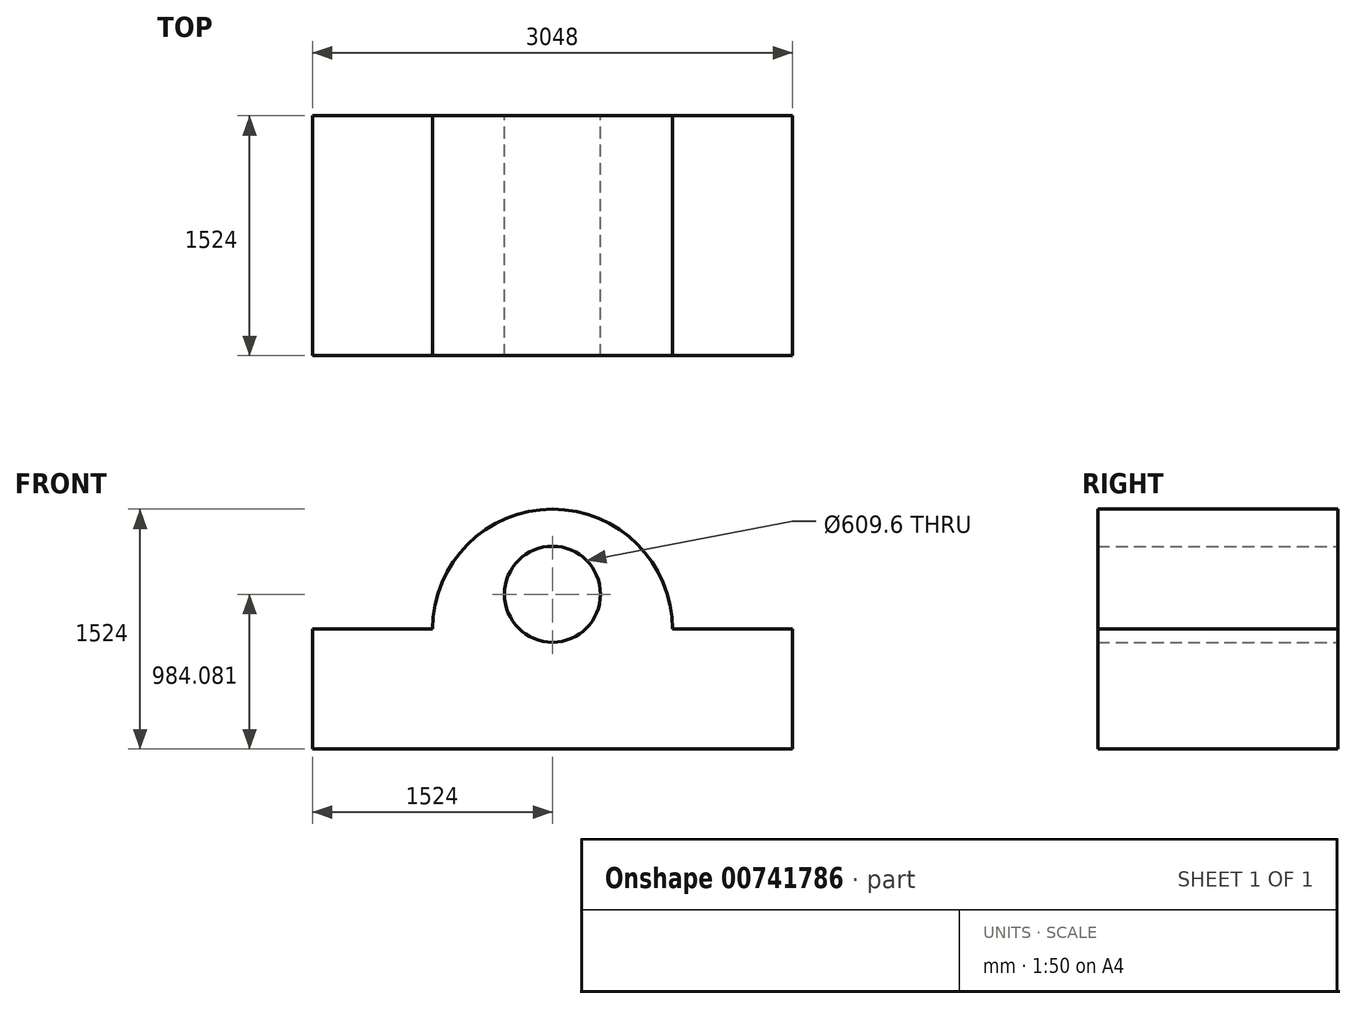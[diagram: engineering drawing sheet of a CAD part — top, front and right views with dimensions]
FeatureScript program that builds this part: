
annotation { "Feature Type Name" : "Feature", "Feature Type Description" : "" }
export const myFeature = defineFeature(function(context is Context, id is Id, definition is map)
    precondition{}
    {
        {
            var Q0;
            Q0=qCreatedBy(makeId("Front.planeOp"),FACE);
            var sketch = newSketch(context, id + "F0", { "sketchPlane" : qUnion([Q0])});
            skLineSegment(sketch, "E0", {"start": v(0, 0) * mm, "end": v(3048, 0) * mm});
            skLineSegment(sketch, "E1", {"start": v(0, 0) * mm, "end": v(0, 762) * mm});
            skLineSegment(sketch, "E2", {"start": v(0, 762) * mm, "end": v(762, 762) * mm});
            skLineSegment(sketch, "E3", {"start": v(3048, 0) * mm, "end": v(3048, 762) * mm});
            skLineSegment(sketch, "E4", {"start": v(3048, 762) * mm, "end": v(2286, 762) * mm});
            skArc(sketch, "E5", {"start": v(2286, 762) * mm, "mid": v(1524, 1524) * mm, "end": v(762, 762) * mm});
            skCircle(sketch, "E6", {"center": v(1524, 984.08) * mm, "radius": 304.8 * mm});
            skSolve(sketch);
        }
        {
            var Q0;
            Q0 = qSketchRegion(id + "F0", true);
            extrude(context, id + "F1", {"entities" : qUnion([Q0]), "depth" : 1524 * mm, "offsetDistance" : 25.4 * mm});
        }
    });
